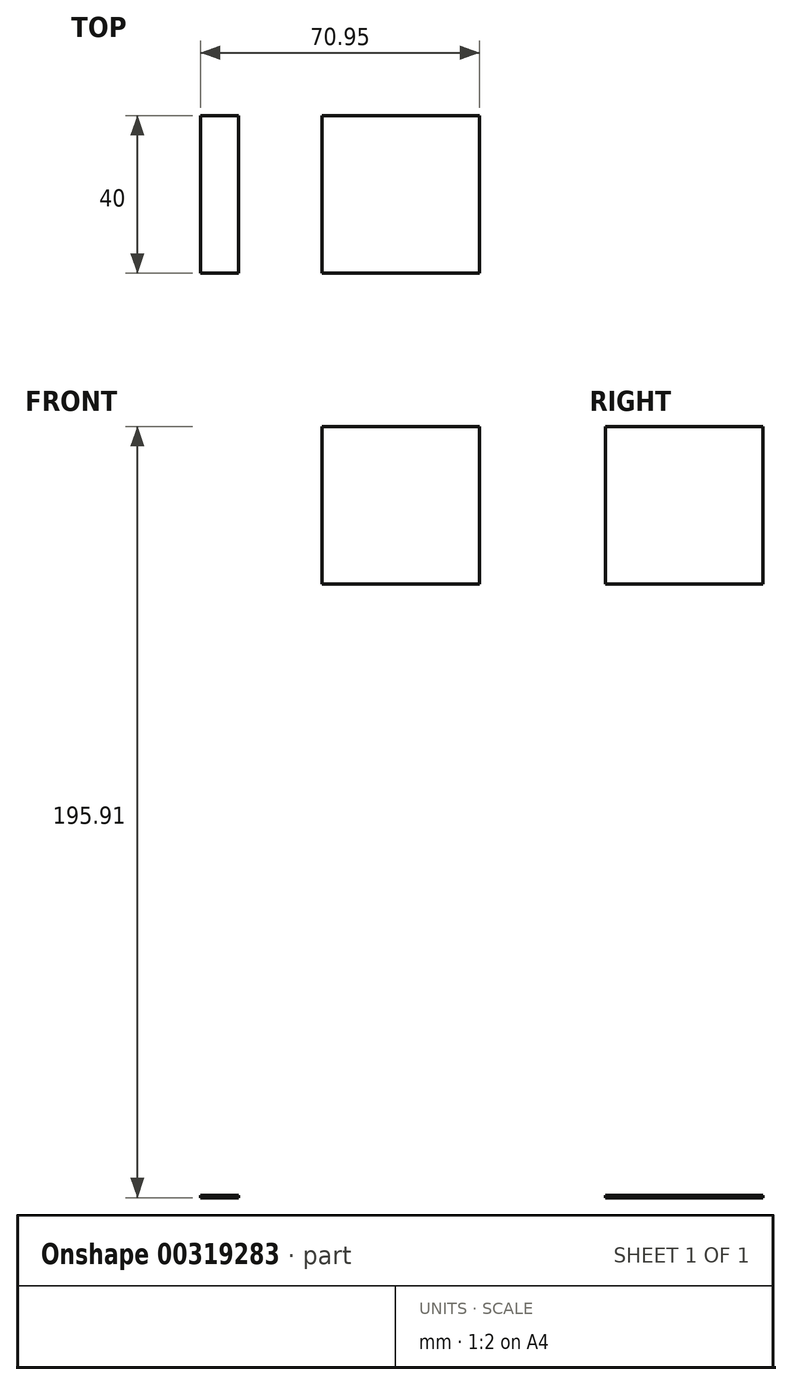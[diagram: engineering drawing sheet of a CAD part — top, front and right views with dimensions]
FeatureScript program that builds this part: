
annotation { "Feature Type Name" : "Feature", "Feature Type Description" : "" }
export const myFeature = defineFeature(function(context is Context, id is Id, definition is map)
    precondition{}
    {
        {
            var Q0;
            Q0=qCreatedBy(makeId("Front.planeOp"),FACE);
            var sketch = newSketch(context, id + "F0", { "sketchPlane" : qUnion([Q0])});
            skLineSegment(sketch, "E0.bottom", {"start": v(-21.31, -155.91) * mm, "end": v(-30.95, -155.91) * mm});
            skLineSegment(sketch, "E0.top", {"start": v(-21.31, -155.33) * mm, "end": v(-30.95, -155.33) * mm});
            skLineSegment(sketch, "E0.left", {"start": v(-21.31, -155.91) * mm, "end": v(-21.31, -155.33) * mm});
            skLineSegment(sketch, "E0.right", {"start": v(-30.95, -155.91) * mm, "end": v(-30.95, -155.33) * mm});
            skLineSegment(sketch, "E1.bottom", {"start": v(0, 0) * mm, "end": v(40, 0) * mm});
            skLineSegment(sketch, "E1.top", {"start": v(0, 40) * mm, "end": v(40, 40) * mm});
            skLineSegment(sketch, "E1.left", {"start": v(0, 0) * mm, "end": v(0, 40) * mm});
            skLineSegment(sketch, "E1.right", {"start": v(40, 0) * mm, "end": v(40, 40) * mm});
            skSolve(sketch);
        }
        {
            var Q0;
            Q0 = qSketchRegion(id + "F0", true);
            extrude(context, id + "F1", {"entities" : qUnion([Q0]), "depth" : 40 * mm});
        }
    });
